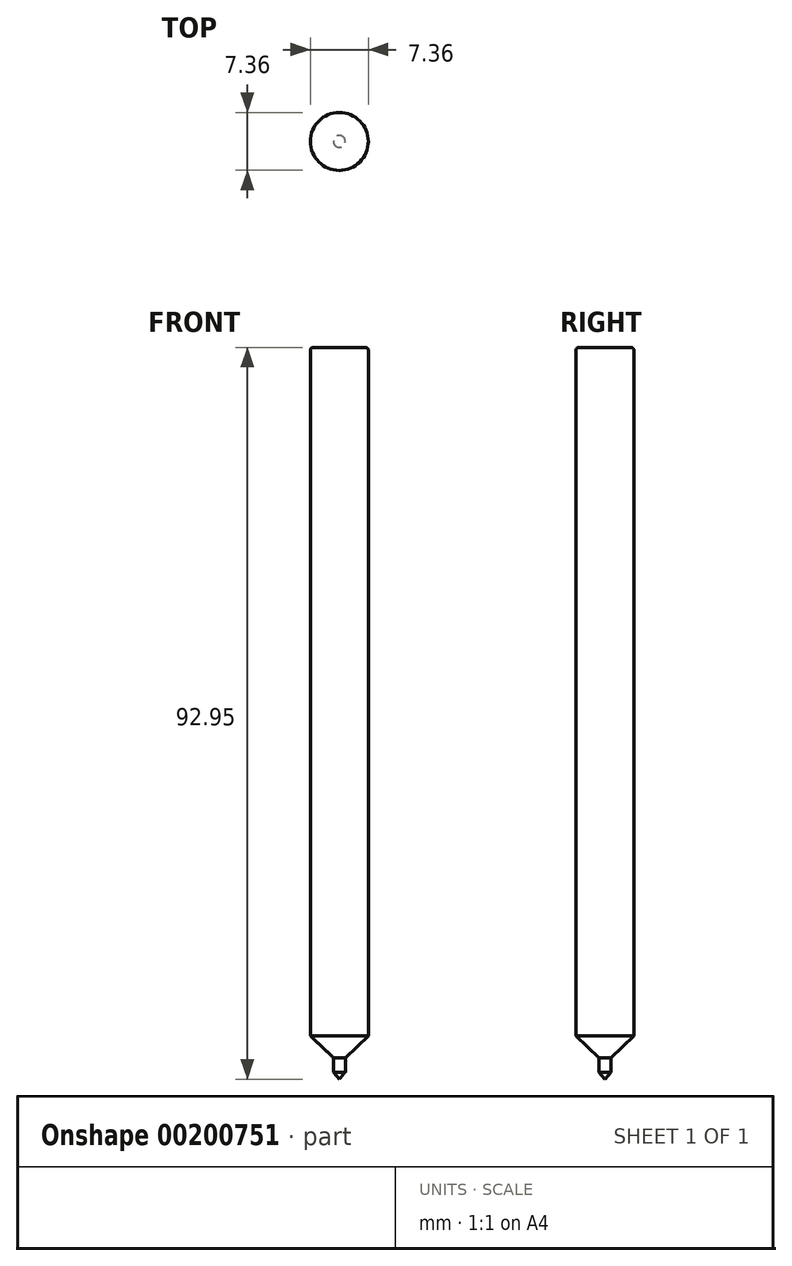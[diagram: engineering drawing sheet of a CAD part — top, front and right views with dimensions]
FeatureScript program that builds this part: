
annotation { "Feature Type Name" : "Feature", "Feature Type Description" : "" }
export const myFeature = defineFeature(function(context is Context, id is Id, definition is map)
    precondition{}
    {
        {
            var Q0;
            Q0=qCreatedBy(makeId("Front.planeOp"),FACE);
            var sketch = newSketch(context, id + "F0", { "sketchPlane" : qUnion([Q0])});
            skLineSegment(sketch, "E0", {"start": v(0, 59.2) * mm, "end": v(3.68, 59.2) * mm});
            skLineSegment(sketch, "E1", {"start": v(3.68, 59.2) * mm, "end": v(3.68, -28.27) * mm});
            skLineSegment(sketch, "E2", {"start": v(0, -33.75) * mm, "end": v(0, 59.2) * mm});
            skLineSegment(sketch, "E3", {"start": v(0, -33.75) * mm, "end": v(0.76, -32.86) * mm});
            skLineSegment(sketch, "E4", {"start": v(0.76, -32.86) * mm, "end": v(0.76, -31.04) * mm});
            skLineSegment(sketch, "E5", {"start": v(3.68, -28.27) * mm, "end": v(0.76, -31.04) * mm});
            skLineSegment(sketch, "E6", {"start": v(3.68, 59.2) * mm, "end": v(3.77, 59.2) * mm});
            skLineSegment(sketch, "E7", {"start": v(3.77, 59.2) * mm, "end": v(3.77, 59.15) * mm});
            skLineSegment(sketch, "E8", {"start": v(3.77, 59.15) * mm, "end": v(3.69, 59.15) * mm});
            skSolve(sketch);
        }
        {
            var Q0;
            Q0 = qSketchRegion(id + "F0", true);
            var Q1;
            Q1=sQuery(id+"F0.wireOp",EDGE,"E2");
            revolve(context, id + "F1", {"entities" : qUnion([Q0]), "axis" : qUnion([Q1]), "revolveType" : RevolveType.FULL});
        }
        {
            var Q0;
            Q0=makeQuery(id+"F1.opRevolve","SWEPT_FACE",FACE,{"disambiguationData":[OSD([sQuery(id+"F0.wireOp",EDGE,"E0")])]});
            fillet(context, id + "F2", {"entities" : qUnion([Q0]), "radius" : 0.37 * mm, "tangentPropagation" : true, "allowEdgeOverflow" : false});
        }
    });
